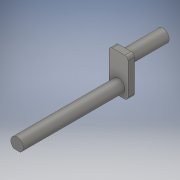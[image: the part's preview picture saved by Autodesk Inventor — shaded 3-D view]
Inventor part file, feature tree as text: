
AUTODESK INVENTOR PART (.ipt)
format: ipt  version: 2018 (Build 220112000, 112)  size: 180,736 bytes
history: native  units: in
note: dims shown in document units (in); Inventor stores cm internally (conversion verified against a paired STEP export)
features: extrude x8, sketch x8, fillet x1, projected_geometry x1
ambient origin geometry x8: Origin, YZ Plane, XZ Plane, XY Plane, X Axis, Y Axis, Z Axis, Center Point
bodies: Solid1 (feature_tree)
feature tree (18):
  extrude  "Extrusion1"  Depth=2.875in
  extrude  "Extrusion2"  Depth=2.0in
  extrude  "Extrusion3"  Depth=0.375in TaperAngle=0.0deg
  extrude  "Extrusion4"  Depth=0.125in
  extrude  "Extrusion5"  Depth=2.0in
  extrude  "Extrusion7"  Depth=0.375in TaperAngle=0.0deg
  extrude  "Extrusion6"  Depth=0.0625in
  fillet  "Fillet1"  Radius=0.375in
  extrude  "Extrusion8"  Depth=0.75in
  sketch  "Sketch1"  dims[d0=0.75in d1=2.875in]
  sketch  "Sketch2"  dims[d2=0.375in d3=0.0in d4=2.0in]
  sketch  "Sketch3"  dims[d6=0.3125in d7=0.375in d8=0.0in]
  sketch  "Sketch4"  dims[d9=0.125in d10=0.3125in]
  sketch  "Sketch5"  dims[d11=0.375in d12=0.0in d13=2.0in]
  sketch  "Sketch6"  dims[d14=0.0625in d15=0.375in d16=0.0in]
  sketch  "Sketch7"  dims[d17=0.75in d18=0.0625in d19=0.375in d20=0.0in]
  sketch  "Sketch8"  dims[d21=0.25in d22=0.143in d23=0.1875in d24=2.0in d25=0.0in d26=0.25in d27=0.1875in d28=0.15in d29=0.75in d30=0.0in d31=0.0625in d32=0.75in d33=0.0in]
  projected_geometry  "Projected Loop1"
